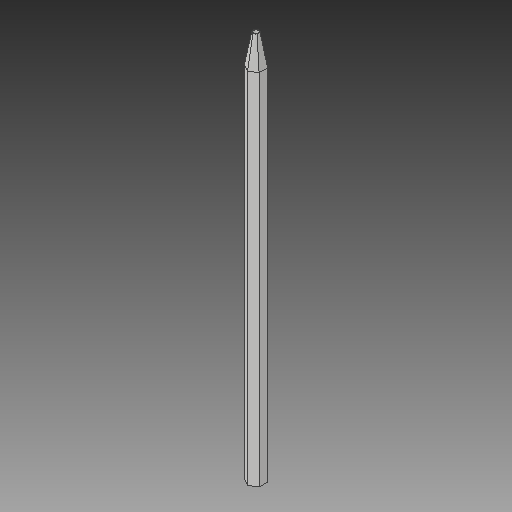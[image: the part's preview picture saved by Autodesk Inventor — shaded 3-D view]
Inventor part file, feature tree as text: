
AUTODESK INVENTOR PART (.ipt)
format: ipt  version: 2017 (Build 210142000, 142)  size: 122,880 bytes
history: native  units: mm
features: sketch x3, extrude x1, plane x1, loft x1, hole x1, other x1
ambient origin geometry x8: Origin, YZ Plane, XZ Plane, XY Plane, X Axis, Y Axis, Z Axis, Center Point
bodies: Solid1 (feature_tree)
feature tree (8):
  extrude  "Extrusion1"  Depth=120.0mm TaperAngle=0.0deg
  plane  "Work Plane1"
  sketch  "Sketch2"  dims[d3=10.0mm d4=4.9mm]
  loft  "Loft1"
  hole  "Hole1"  [1 undecoded]
  sketch  "Sketch1"  dims[d0=4.9mm d1=120.0mm d2=0.0mm]
  sketch  "Sketch3"  dims[d5=2.0mm d6=0.0mm d7=90.0deg d8=0.0mm d9=90.0deg d10=10.0mm d11=10.0mm d12=1.5mm d13=6.0mm d14=4.0mm d15=2.0mm d16=90.0deg d17=8.0mm d18=20.594885mm]
  other  "Edges1"
note: 1 required parameter value undecoded (feature->parameter linkage not recoverable at this tier; creation-order binding heuristic only, values carry confidence <= 0.55)
